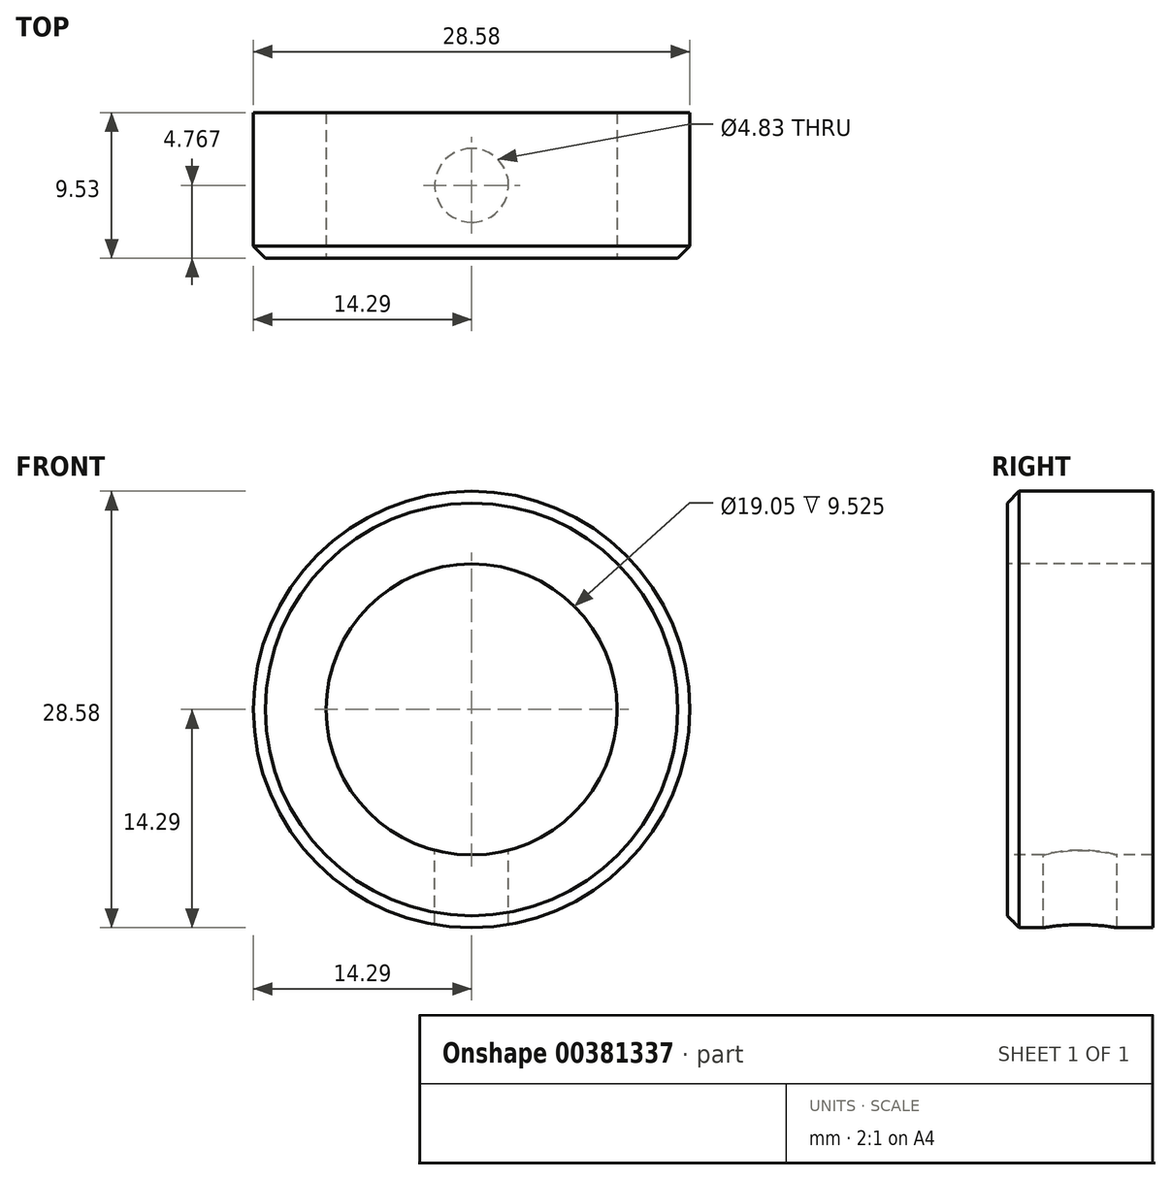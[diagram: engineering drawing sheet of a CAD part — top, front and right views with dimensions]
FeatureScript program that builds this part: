
annotation { "Feature Type Name" : "Feature", "Feature Type Description" : "" }
export const myFeature = defineFeature(function(context is Context, id is Id, definition is map)
    precondition{}
    {
        {
            var Q0;
            Q0=qCreatedBy(makeId("Front.planeOp"),FACE);
            var sketch = newSketch(context, id + "F0", { "sketchPlane" : qUnion([Q0])});
            skCircle(sketch, "E0", {"center": v(0, 0) * mm, "radius": 14.29 * mm});
            skSolve(sketch);
        }
        {
            var Q0;
            Q0=makeQuery(id+"F0.imprint","IMPRINT",FACE,{"disambiguationData":[TD([[makeQuery(id+"F0.imprint","IMPRINT",EDGE,{"derivedFrom":sQuery(id+"F0.wireOp",EDGE,"E0")}),1.0]])]});
            extrude(context, id + "F1", {"entities" : qUnion([Q0]), "depth" : 9.52 * mm});
        }
        {
            var Q0;
            Q0=makeQuery(id+"F1.opExtrude","CAP_FACE",FACE,{"disambiguationData":[OSD([sQuery(id+"F0.wireOp",EDGE,"E0")])],"isStart":false});
            var sketch = newSketch(context, id + "F2", { "sketchPlane" : qUnion([Q0])});
            skCircle(sketch, "E1", {"center": v(0, 0) * mm, "radius": 9.53 * mm});
            skSolve(sketch);
        }
        {
            var Q0;
            Q0=makeQuery(id+"F2.imprint","IMPRINT",FACE,{"disambiguationData":[TD([[makeQuery(id+"F2.imprint","IMPRINT",EDGE,{"derivedFrom":sQuery(id+"F2.wireOp",EDGE,"E1")}),1.0]])]});
            extrude(context, id + "F3", {"entities" : qUnion([Q0]), "operationType" : NewBodyOperationType.REMOVE, "endBound" : BoundingType.UP_TO_NEXT, "oppositeDirection" : true, "depth" : 25.4 * mm});
        }
        {
            var Q0;
            Q0=qCreatedBy(makeId("Top.planeOp"),FACE);
            var sketch = newSketch(context, id + "F4", { "sketchPlane" : qUnion([Q0])});
            skCircle(sketch, "E2", {"center": v(0, -4.76) * mm, "radius": 2.41 * mm});
            skSolve(sketch);
        }
        {
            var Q0;
            Q0=qSketchRegion(id+"F4",true);
            extrude(context, id + "F5", {"entities" : qUnion([Q0]), "operationType" : NewBodyOperationType.REMOVE, "oppositeDirection" : true, "depth" : 25.4 * mm});
        }
        {
            var Q0;
            Q0=makeQuery(id+"F1.opExtrude","CAP_EDGE",EDGE,{"disambiguationData":[OSD([sQuery(id+"F0.wireOp",EDGE,"E0")])],"isStart":false});
            chamfer(context, id + "F6", {"entities" : qUnion([Q0]), "chamferType" : ChamferType.OFFSET_ANGLE, "width" : 0.79 * mm, "oppositeDirection" : false, "angle" : 45 * degree, "tangentPropagation" : true});
        }
    });
